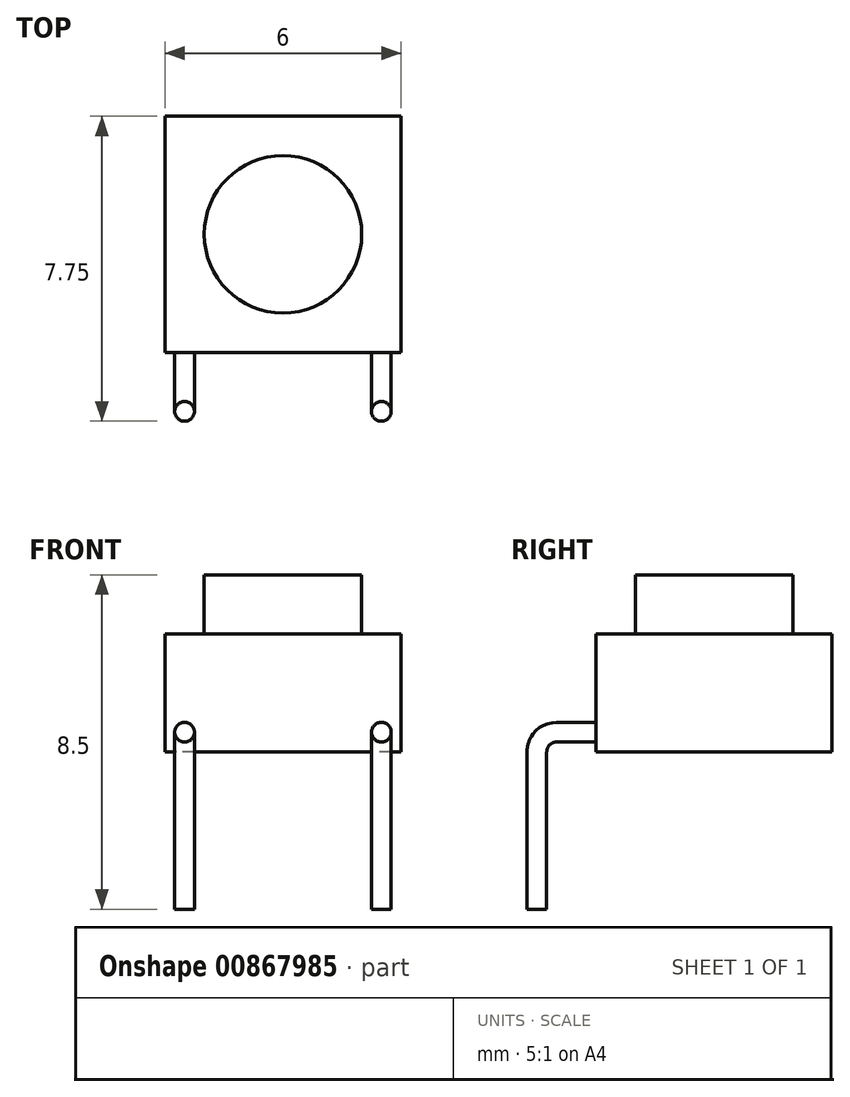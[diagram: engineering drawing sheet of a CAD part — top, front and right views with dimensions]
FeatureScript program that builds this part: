
annotation { "Feature Type Name" : "Feature", "Feature Type Description" : "" }
export const myFeature = defineFeature(function(context is Context, id is Id, definition is map)
    precondition{}
    {
        {
            var Q0;
            Q0=qCreatedBy(makeId("Top.planeOp"),FACE);
            var sketch = newSketch(context, id + "F0", { "sketchPlane" : qUnion([Q0])});
            skLineSegment(sketch, "E0.bottom", {"start": v(3, 3) * mm, "end": v(-3, 3) * mm});
            skLineSegment(sketch, "E0.top", {"start": v(3, -3) * mm, "end": v(-3, -3) * mm});
            skLineSegment(sketch, "E0.left", {"start": v(3, 3) * mm, "end": v(3, -3) * mm});
            skLineSegment(sketch, "E0.right", {"start": v(-3, 3) * mm, "end": v(-3, -3) * mm});
            skPoint(sketch, "E0.middle", {"position": v(0, 0) * mm});
            skSolve(sketch);
        }
        {
            var Q0;
            Q0 = qSketchRegion(id + "F0", true);
            extrude(context, id + "F1", {"entities" : qUnion([Q0]), "depth" : 3 * mm, "offsetDistance" : 25 * mm});
        }
        {
            var Q0;
            Q0=makeQuery(id+"F1.opExtrude","CAP_FACE",FACE,{"disambiguationData":[OSD([sQuery(id+"F0.wireOp",EDGE,"E0.bottom"),sQuery(id+"F0.wireOp",EDGE,"E0.top"),sQuery(id+"F0.wireOp",EDGE,"E0.left"),sQuery(id+"F0.wireOp",EDGE,"E0.right")])],"isStart":false});
            var sketch = newSketch(context, id + "F2", { "sketchPlane" : qUnion([Q0])});
            skCircle(sketch, "E1", {"center": v(0, 0) * mm, "radius": 2 * mm});
            skSolve(sketch);
        }
        {
            var Q0;
            Q0 = qSketchRegion(id + "F2", true);
            extrude(context, id + "F3", {"entities" : qUnion([Q0]), "operationType" : NewBodyOperationType.ADD, "depth" : 1.5 * mm, "offsetDistance" : 25 * mm});
        }
        {
            var Q0;
            Q0=makeQuery(id+"F1.opExtrude","SWEPT_FACE",FACE,{"disambiguationData":[OSD([sQuery(id+"F0.wireOp",EDGE,"E0.top")])]});
            var sketch = newSketch(context, id + "F4", { "sketchPlane" : qUnion([Q0])});
            skCircle(sketch, "E2", {"center": v(-2.5, 0.5) * mm, "radius": 0.25 * mm});
            skCircle(sketch, "E3", {"center": v(2.5, 0.5) * mm, "radius": 0.25 * mm});
            skSolve(sketch);
        }
        {
            var Q0;
            Q0=makeQuery(id+"F1.opExtrude","SWEPT_FACE",FACE,{"disambiguationData":[OSD([sQuery(id+"F0.wireOp",EDGE,"E0.right")])]});
            var sketch = newSketch(context, id + "F5", { "sketchPlane" : qUnion([Q0])});
            skLineSegment(sketch, "E4", {"start": v(3, 0.7) * mm, "end": v(4, 0.7) * mm});
            skArc(sketch, "E5", {"start": v(4.7, 0) * mm, "mid": v(4.5, 0.5) * mm, "end": v(4, 0.7) * mm});
            skLineSegment(sketch, "E6", {"start": v(4.7, 0) * mm, "end": v(4.7, -4) * mm});
            skSolve(sketch);
        }
        {
            var Q0;
            Q0=makeQuery(id+"F4.imprint","IMPRINT",FACE,{"disambiguationData":[TD([[makeQuery(id+"F4.imprint","IMPRINT",EDGE,{"derivedFrom":sQuery(id+"F4.wireOp",EDGE,"E2")}),1.0]])]});
            var Q1;
            Q1=makeQuery(id+"F4.imprint","IMPRINT",FACE,{"disambiguationData":[TD([[makeQuery(id+"F4.imprint","IMPRINT",EDGE,{"derivedFrom":sQuery(id+"F4.wireOp",EDGE,"E3")}),1.0]])]});
            var Q2;
            Q2=sQuery(id+"F5.wireOp",EDGE,"E4");
            var Q3;
            Q3=sQuery(id+"F5.wireOp",EDGE,"E5");
            var Q4;
            Q4=sQuery(id+"F5.wireOp",EDGE,"E6");
            sweep(context, id + "F6", {"operationType" : NewBodyOperationType.ADD, "profiles" : qUnion([Q0, Q1]), "path" : qUnion([Q2, Q3, Q4])});
        }
    });
